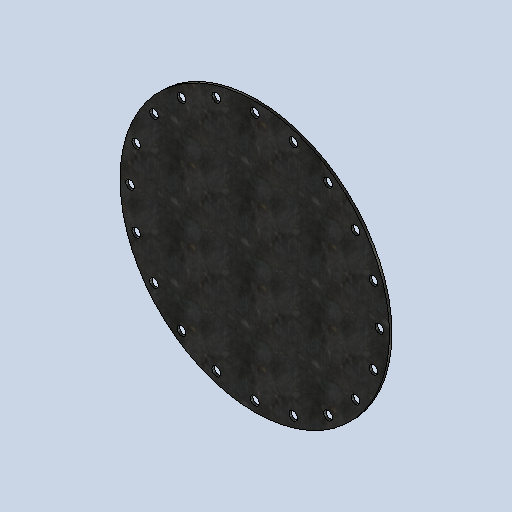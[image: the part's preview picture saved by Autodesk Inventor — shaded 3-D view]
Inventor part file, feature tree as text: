
AUTODESK INVENTOR PART (.ipt)
format: ipt  version: 2025.1 (Build 291241020, 241B)  size: 256,512 bytes
history: native  units: mm
features: sketch x2, other x2, extrude x1, pattern_circular x1
ambient origin geometry x8: Origin, YZ Plane, XZ Plane, XY Plane, X Axis, Y Axis, Z Axis, Center Point
bodies: Solid1 (feature_tree)
feature tree (6):
  extrude  "Extrusion1"  Depth=6.0mm TaperAngle=0.0deg
  pattern_circular  "Circular Pattern1"  Count=62  [1 undecoded]
  sketch  "Sketch1"  dims[d0=670.0mm d1=6.0mm d2=0.0mm]
  sketch  "Sketch2"  dims[d3=22.0mm d4=620.0mm d5=6.0mm d6=6.0mm d7=0.0mm d8=200.0mm d9=360.0deg]
  other  "Cut1"
  other  "Definition1"
note: 1 required parameter value undecoded (feature->parameter linkage not recoverable at this tier; creation-order binding heuristic only, values carry confidence <= 0.55)
